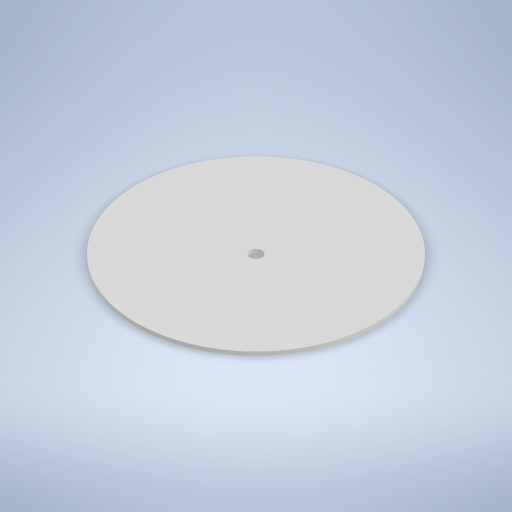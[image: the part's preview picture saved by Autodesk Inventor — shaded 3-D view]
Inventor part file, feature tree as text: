
AUTODESK INVENTOR PART (.ipt)
format: ipt  version: 2024 (Build 280153000, 153)  size: 224,256 bytes
history: native  units: mm
features: sketch x2, extrude x1, hole x1
ambient origin geometry x8: Origin, YZ Plane, XZ Plane, XY Plane, X Axis, Y Axis, Z Axis, Center Point
bodies: Volumenkörper1 (feature_tree)
feature tree (4):
  extrude  "Extrusion1"  Depth=0.5mm TaperAngle=0.0deg
  hole  "Bohrung1"  [1 undecoded]
  sketch  "Skizze1"  dims[d0=32.5mm d1=0.5mm d2=0.0mm]
  sketch  "Skizze2"  dims[d3=1.65mm d4=30.0mm d5=4.0mm d6=2.0mm d7=90.0deg d8=8.0mm d9=0.0mm]
note: 1 required parameter value undecoded (feature->parameter linkage not recoverable at this tier; creation-order binding heuristic only, values carry confidence <= 0.55)
